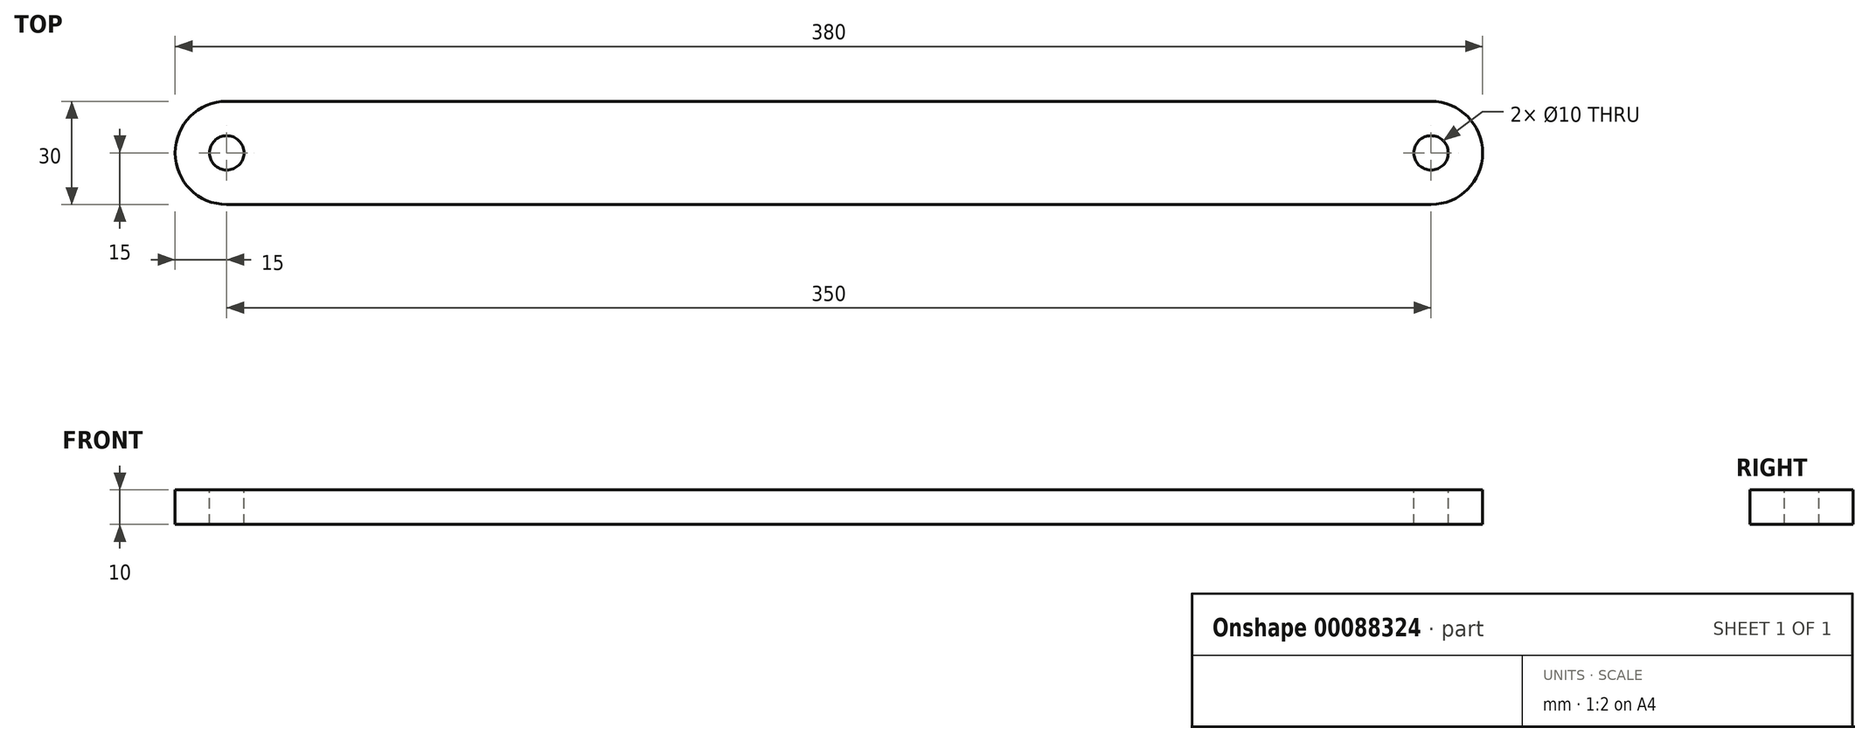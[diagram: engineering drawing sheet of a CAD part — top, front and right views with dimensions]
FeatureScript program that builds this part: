
annotation { "Feature Type Name" : "Feature", "Feature Type Description" : "" }
export const myFeature = defineFeature(function(context is Context, id is Id, definition is map)
    precondition{}
    {
        {
            var Q0;
            Q0=qCreatedBy(makeId("Top.planeOp"),FACE);
            var sketch = newSketch(context, id + "F0", { "sketchPlane" : qUnion([Q0])});
            skLineSegment(sketch, "E0", {"start": v(0, 15) * mm, "end": v(350, 15) * mm});
            skArc(sketch, "E1", {"start": v(350, 15) * mm, "mid": v(365, 0) * mm, "end": v(350, -15) * mm});
            skArc(sketch, "E2", {"start": v(0, 15) * mm, "mid": v(-15, 0) * mm, "end": v(0, -15) * mm});
            skLineSegment(sketch, "E3", {"start": v(0, -15) * mm, "end": v(350, -15) * mm});
            skSolve(sketch);
        }
        {
            var Q0;
            Q0 = qSketchRegion(id + "F0", true);
            extrude(context, id + "F1", {"entities" : qUnion([Q0]), "depth" : 10 * mm});
        }
        {
            var Q0;
            Q0=makeQuery(id+"F1.opExtrude","CAP_FACE",FACE,{"disambiguationData":[OSD([sQuery(id+"F0.wireOp",EDGE,"E0"),sQuery(id+"F0.wireOp",EDGE,"E1"),sQuery(id+"F0.wireOp",EDGE,"E2"),sQuery(id+"F0.wireOp",EDGE,"E3")])],"isStart":false});
            var sketch = newSketch(context, id + "F2", { "sketchPlane" : qUnion([Q0])});
            skCircle(sketch, "E4", {"center": v(0, 0) * mm, "radius": 5 * mm});
            skCircle(sketch, "E5", {"center": v(350, 0) * mm, "radius": 5 * mm});
            skSolve(sketch);
        }
        {
            var Q0;
            Q0 = qSketchRegion(id + "F2", true);
            extrude(context, id + "F3", {"entities" : qUnion([Q0]), "operationType" : NewBodyOperationType.REMOVE, "endBound" : BoundingType.THROUGH_ALL, "oppositeDirection" : true, "depth" : 25 * mm});
        }
    });
